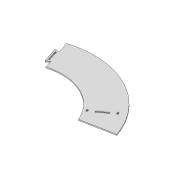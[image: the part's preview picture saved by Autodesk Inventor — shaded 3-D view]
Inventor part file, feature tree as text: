
AUTODESK INVENTOR PART (.ipt)
format: ipt  version: 2020 (Build 240168000, 168)  size: 266,240 bytes
history: native  units: mm
features: extrude x1, sketch x1
ambient origin geometry x8: Origin, YZ Plane, XZ Plane, XY Plane, X Axis, Y Axis, Z Axis, Center Point
bodies: Solid1 (feature_tree)
feature tree (2):
  extrude  "Extrusion1"  Depth=1.75mm
  sketch  "Sketch1"  dims[d0=504.787567mm d1=944.787567mm d34=1152.87mm d45=7.5mm d48=712.87mm d52=7.0mm d53=0.0mm d58=50.0mm d60=360.0deg d62=13.601997mm d63=25.0mm d65=50.0mm d71=50.0mm d72=7.5mm d74=3.5mm d75=3.5mm d79=0.0mm d80=8.0mm d81=1.75mm d83=50.0mm d84=8.0mm d85=1.75mm d86=50.0mm d88=360.0deg]
